# Revit family: 631-00-001-DN50-700
name_source: partatom
category: Pipe Accessories
units: mm (PartAtom-declared; Revit-internal decimal feet)

## family parameters
Always vertical = No
Cut with Voids When Loaded = No
Part Type = Valve - Breaks Into
Round Connector Dimension = Use Diameter
Shared = No
Work Plane-Based = No

## types (16) — shared parameters
Body_wallthickness = 10 mm  [stored 0.0328084 ft]
DN050_PN16 = 631-071-00-6
DN065_PN16 = 631-091-00-6
DN080_PN 16 = 631-106-00-6
DN100_PN16 = 631-133-00-6
DN125_PN16 = 631-161-00-6
DN150_PN16 = 631-188-00-6
DN200_PN16 = 631-227-00-6
DN225_PN16 = 631-257-00-6
DN250_PN16 = 631-301-00-6
DN300_PN16 = 631-356-00-6
DN350_PN16 = 631-396-00-6
DN400_PN16 = 631-442-00-6
DN450_PN16 = 631-510-00-6
DN500_PN16 = 631-552-00-6
DN600_PN16 = 631-652-00-6
DN700_PN16 = 631-745-00-6
Description_ = AVK SUPA MAXI™ STRAIGHT COUPLING
Search_table = 631-00-001-DN50-700
URL product pages = https://www.avkvalves.com

## per-type parameters (varying)
| type | D | DN | DN_ref | Flange_thickness | H3 | H3_Ref | ID | L | L_ref | Seal_range | Seal_range_ref |
| DN050_PN16 | 200 mm | 50 mm  [stored 0.164042 ft] | 27 mm  [stored 0.0885827 ft] | 9.5 mm  [stored 0.031168 ft] | 82.5 mm  [stored 0.270669 ft] | 45 mm  [stored 0.147638 ft] | 25 mm  [stored 0.082021 ft] | 255 mm | 127.5 mm | 30 mm  [stored 0.0984252 ft] | 60 mm  [stored 0.19685 ft] |
| DN065_PN16 | 226 mm | 65 mm  [stored 0.213255 ft] | 37 mm  [stored 0.121391 ft] | 9.5 mm  [stored 0.031168 ft] | 92.5 mm  [stored 0.303478 ft] | 55 mm  [stored 0.180446 ft] | 32.5 mm  [stored 0.106627 ft] | 265 mm | 132.5 mm | 40 mm  [stored 0.131234 ft] | 80 mm  [stored 0.262467 ft] |
| DN080_PN 16 | 235 mm | 80 mm  [stored 0.262467 ft] | 44 mm  [stored 0.144357 ft] | 9.5 mm  [stored 0.031168 ft] | 100 mm  [stored 0.328084 ft] | 62 mm  [stored 0.203412 ft] | 40 mm  [stored 0.131234 ft] | 268 mm | 134 mm | 47 mm  [stored 0.154199 ft] | 94 mm  [stored 0.308399 ft] |
| DN100_PN16 | 268 mm | 100 mm  [stored 0.328084 ft] | 56.5 mm  [stored 0.185367 ft] | 9.5 mm  [stored 0.031168 ft] | 114.5 mm | 74.5 mm  [stored 0.244423 ft] | 50 mm  [stored 0.164042 ft] | 289 mm | 144.5 mm | 59.5 mm  [stored 0.19521 ft] | 119 mm |
| DN125_PN16 | 285 mm | 125 mm | 70 mm  [stored 0.229659 ft] | 9.5 mm  [stored 0.031168 ft] | 100 mm  [stored 0.328084 ft] | 88 mm  [stored 0.288714 ft] | 62.5 mm  [stored 0.205052 ft] | 277 mm | 138.5 mm | 73 mm  [stored 0.239501 ft] | 146 mm |
| DN150_PN16 | 340 mm | 150 mm | 84 mm  [stored 0.275591 ft] | 9.5 mm  [stored 0.031168 ft] | 114.5 mm | 102 mm  [stored 0.334646 ft] | 75 mm | 314 mm | 157 mm | 87 mm  [stored 0.285433 ft] | 174 mm |
| DN200_PN16 | 389 mm | 200 mm | 102 mm  [stored 0.334646 ft] | 9.5 mm  [stored 0.031168 ft] | 142.5 mm | 120 mm | 100 mm  [stored 0.328084 ft] | 354 mm | 177 mm | 105 mm  [stored 0.344488 ft] | 210 mm |
| DN225_PN16 | 437 mm | 225 mm | 117.5 mm | 10 mm  [stored 0.0328084 ft] | 142.5 mm | 135.5 mm | 112.5 mm | 390 mm | 195 mm | 120.5 mm | 241 mm |
| DN250_PN16 | 476 mm | 250 mm | 139 mm | 11 mm  [stored 0.0360892 ft] | 171.5 mm | 157 mm | 125 mm | 381 mm | 190.5 mm | 142 mm | 284 mm |
| DN300_PN16 | 545 mm | 300 mm | 164.5 mm | 12.25 mm  [stored 0.0401903 ft] | 203 mm | 182.5 mm | 150 mm | 438 mm | 219 mm | 167.5 mm | 335 mm |
| DN350_PN16 | 612 mm | 350 mm | 185 mm | 13.25 mm  [stored 0.0434711 ft] | 171.5 mm | 203 mm | 175 mm | 513 mm | 256.5 mm | 188 mm | 376 mm |
| DN400_PN16 | 661 mm | 400 mm | 205.5 mm | 14 mm  [stored 0.0459318 ft] | 203 mm | 223.5 mm | 200 mm | 526 mm | 263 mm | 208.5 mm | 417 mm |
| DN450_PN16 | 740 mm | 450 mm | 236.5 mm | 15 mm  [stored 0.0492126 ft] | 241.5 mm | 254.5 mm | 225 mm | 767 mm | 383.5 mm | 239.5 mm | 479 mm |
| DN500_PN16 | 772 mm | 500 mm | 259.5 mm | 15.75 mm  [stored 0.0516732 ft] | 270 mm | 277.5 mm | 250 mm | 769 mm | 384.5 mm | 262.5 mm | 525 mm |
| DN600_PN16 | 872 mm | 600 mm | 311 mm | 15.75 mm  [stored 0.0516732 ft] | 298.5 mm | 329 mm | 300 mm | 767 mm | 383.5 mm | 314 mm | 628 mm |
| DN700_PN16 | 991 mm | 700 mm | 358.5 mm | 18 mm  [stored 0.0590551 ft] | 330 mm | 376.5 mm | 350 mm | 745 mm | 372.5 mm | 361.5 mm | 723 mm |

note: [stored X ft] marks values corroborated as IEEE doubles in the binary element streams (Revit-internal decimal feet)

## geometry (parser evidence)
native form markers: Sweep x9
no freeform markers — native parametric forms only
